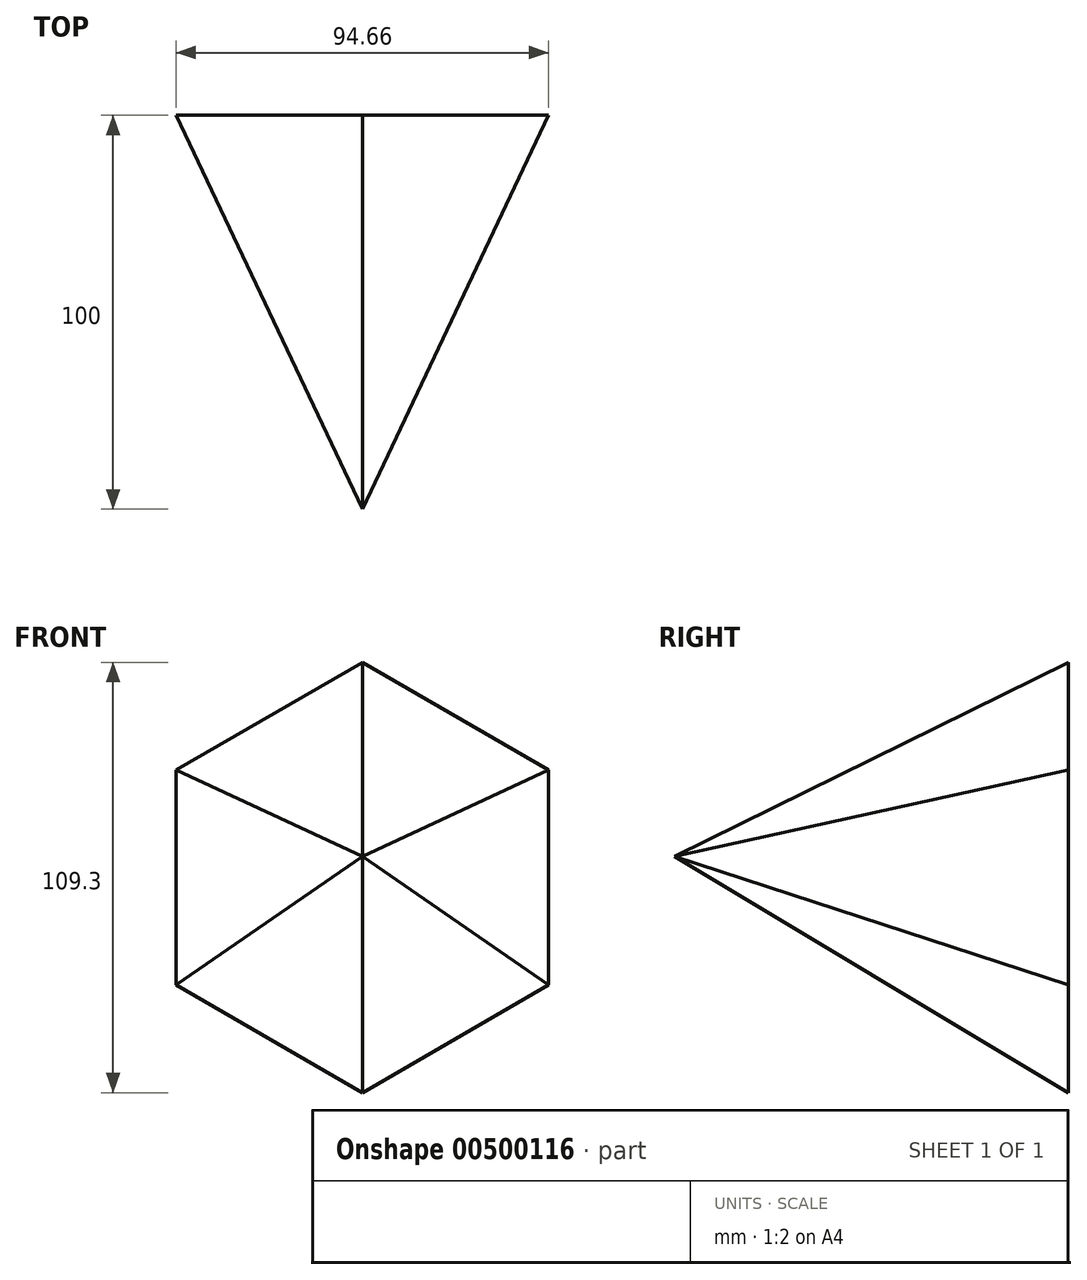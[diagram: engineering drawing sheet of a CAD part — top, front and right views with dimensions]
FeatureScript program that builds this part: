
annotation { "Feature Type Name" : "Feature", "Feature Type Description" : "" }
export const myFeature = defineFeature(function(context is Context, id is Id, definition is map)
    precondition{}
    {
        {
            var Q0;
            Q0=qCreatedBy(makeId("Front.planeOp"),FACE);
            var sketch = newSketch(context, id + "F0", { "sketchPlane" : qUnion([Q0])});
            skCircle(sketch, "E0.cCircle", {"center": v(0, 0) * mm, "radius": 54.65 * mm, "construction": true});
            skLineSegment(sketch, "E0.0", {"start": v(0, 54.65) * mm, "end": v(47.33, 27.33) * mm});
            skLineSegment(sketch, "E0.1", {"start": v(47.33, 27.33) * mm, "end": v(47.33, -27.33) * mm});
            skLineSegment(sketch, "E0.2", {"start": v(47.33, -27.33) * mm, "end": v(0, -54.65) * mm});
            skLineSegment(sketch, "E0.3", {"start": v(0, -54.65) * mm, "end": v(-47.33, -27.33) * mm});
            skLineSegment(sketch, "E0.4", {"start": v(-47.33, -27.33) * mm, "end": v(-47.33, 27.33) * mm});
            skLineSegment(sketch, "E0.5", {"start": v(-47.33, 27.33) * mm, "end": v(0, 54.65) * mm});
            skSolve(sketch);
        }
        {
            var Q0;
            Q0=qCreatedBy(makeId("Front.planeOp"),FACE);
            cPlane(context, id + "F1", {"entities" : qUnion([Q0]), "cplaneType" : CPlaneType.OFFSET, "offset" : 100 * mm, "width" : 150 * mm, "height" : 150 * mm});
        }
        {
            var Q0;
            Q0=qCreatedBy(id+"F1.planeOp",FACE);
            var sketch = newSketch(context, id + "F2", { "sketchPlane" : qUnion([Q0])});
            skPoint(sketch, "E1", {"position": v(0, 5.43) * mm});
            skSolve(sketch);
        }
        {
            var Q0;
            Q0=makeQuery(id+"F0.imprint","IMPRINT",FACE,{"disambiguationData":[TD([[makeQuery(id+"F0.imprint","IMPRINT",EDGE,{"derivedFrom":sQuery(id+"F0.wireOp",EDGE,"E0.0")}),-1.0]])]});
            var Q1;
            Q1=sQuery(id+"F2.wireOp",VERTEX,"E1");
            loft(context, id + "F3", {"sheetProfilesArray" : [{ "sheetProfileEntities" : qUnion([Q0]) }, { "sheetProfileEntities" : qUnion([Q1]) }]});
        }
    });
